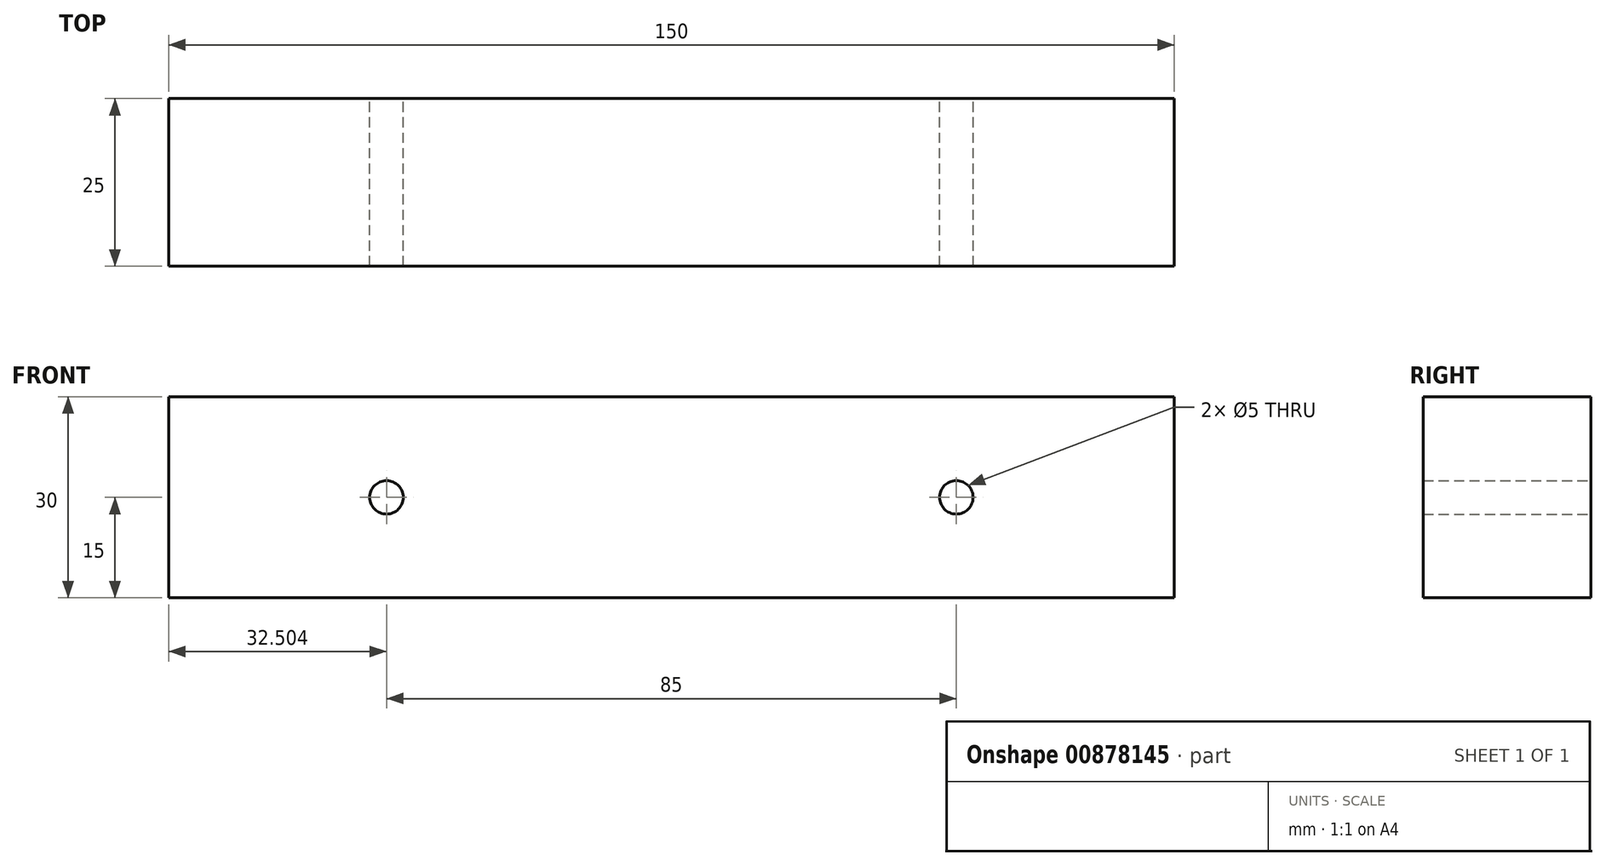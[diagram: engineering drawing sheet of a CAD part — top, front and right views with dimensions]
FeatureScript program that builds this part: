
annotation { "Feature Type Name" : "Feature", "Feature Type Description" : "" }
export const myFeature = defineFeature(function(context is Context, id is Id, definition is map)
    precondition{}
    {
        {
            var Q0;
            Q0=qCreatedBy(makeId("Front.planeOp"),FACE);
            var sketch = newSketch(context, id + "F0", { "sketchPlane" : qUnion([Q0])});
            skCircle(sketch, "E0", {"center": v(-77.26, 0) * mm, "radius": 2.5 * mm});
            skCircle(sketch, "E1", {"center": v(7.74, 0) * mm, "radius": 2.5 * mm});
            skLineSegment(sketch, "E2.bottom", {"start": v(-109.76, 15) * mm, "end": v(40.24, 15) * mm});
            skLineSegment(sketch, "E2.top", {"start": v(-109.76, -15) * mm, "end": v(40.24, -15) * mm});
            skLineSegment(sketch, "E2.left", {"start": v(-109.76, 15) * mm, "end": v(-109.76, -15) * mm});
            skLineSegment(sketch, "E2.right", {"start": v(40.24, 15) * mm, "end": v(40.24, -15) * mm});
            skPoint(sketch, "E2.middle", {"position": v(-34.76, 0) * mm});
            skPoint(sketch, "E3.orphan", {"position": v(-79.76, 0) * mm});
            skPoint(sketch, "E4.orphan", {"position": v(10.24, 0) * mm});
            skSolve(sketch);
        }
        {
            var Q0;
            Q0 = qSketchRegion(id + "F0", true);
            extrude(context, id + "F1", {"entities" : qUnion([Q0]), "depth" : 25 * mm, "offsetDistance" : 25 * mm});
        }
    });
